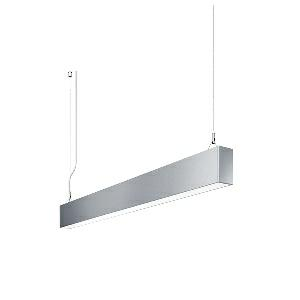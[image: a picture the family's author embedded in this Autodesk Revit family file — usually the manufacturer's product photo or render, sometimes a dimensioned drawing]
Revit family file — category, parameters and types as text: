
# Revit family: idoo_line_-_ilp_3000_840_d_00805674_4773
name_source: partatom
category: Lighting Fixtures
units: mm (PartAtom-declared; Revit-internal decimal feet)

## family parameters
Cut with Voids When Loaded = No
Host = Face
Light Source = No
Part Type = Normal
Room Calculation Point = No
Round Connector Dimension = Use Diameter
Shared = No

## types (1)
- IDOO.line - ILP 3000/840/D (1 x LED, 3150 lm, 4000K)
    Apparent Load = 23 VA
    Approval mark = CE
    CIE Flux Codes = 66 91 98 40 100
    Color Rendering = 80-89
    Color Temperature = 4000K
    Control Gear = Electronic ballast
    Default Elevation = 1800 mm
    Description = ILP 3000/840/D|Suspended luminaire|light source: LED|connected load: 220-240 V, 50/60 Hz|Power consumption: approx. 23 W|standby: approx. 0,20|luminous flux: 3150 lm|luminous efficacy: 136 lm/W|light distribution: Direct/indirect|direct ratio: approx. 40 %|colour temperature: Cold white, ca. 4000 K|color rendering index (CRI): >= 80|chromaticity tolerance:  3 SDCM|System of protection: IP 40|technology: Continuously dimmable|luminaire body|material: Sectional aluminium|colour: Silver|lamp cover: Acrylic (PMMA), Clear|mains lead: 2.00 m With free stranded wires|Fastening: Steel cable 0.3 - 0.7 m|glare control: Prism aperture|luminance(L65): <= 2700 cd/m|unified glare rating(4H 8H): <=  16|special features: DALI Load 1x, TouchDIM - dimming via standard switch, Flicker-free, Suitable as emergency lighting|
    Frequency = 50 Hz
    Height = 110 mm
    Lamp = 1 x LED
    Lamp Light Flux = 3150 lm
    Lamp count = 1
    Length = 1134 mm
    Luminous efficacy = 137 lm/W
    Manufacturer = Waldmann
    ModVariant = No
    Model = 00805674
    Mounting Place = Ceiling
    Mounting Type = Pendant
    Number of Poles = 1
    OnlyDefault = Yes
    Power Factor = 1
    Product Name = IDOO.line - ILP 3000/840/D
    Product group = Suspended luminaire
    ProductGroupID = 9
    Protection Class = Protection class I
    Protection Degree = IP 40
    RLX_Detail_Level = 1
    RLX_Emergency_Light_Flux = 0 lm
    RLX_Emergency_Type = 0
    RLX_Emergency_Type_DB = No
    RlxData = <blob elided: 20845 chars, md5=54d5cdff>
    Socket = socket
    Standby Power = 0 W
    System Light Flux = 3150 lm
    System Power = 23 W
    Type Comments = Product without accessories
    Type Image = 113290000-00692519.jpg
    URL = http://relux.com
    VarID = ---
    Voltage = 230 V
    Voltage Range = 220-240 V
    Weight = 0.00 kg
    Width = 60 mm  [stored 0.19685 ft]

note: [stored X ft] marks values corroborated as IEEE doubles in the binary element streams (Revit-internal decimal feet)

## geometry (parser evidence)
native form markers: Blend x4, Sweep x12
no freeform markers — native parametric forms only
